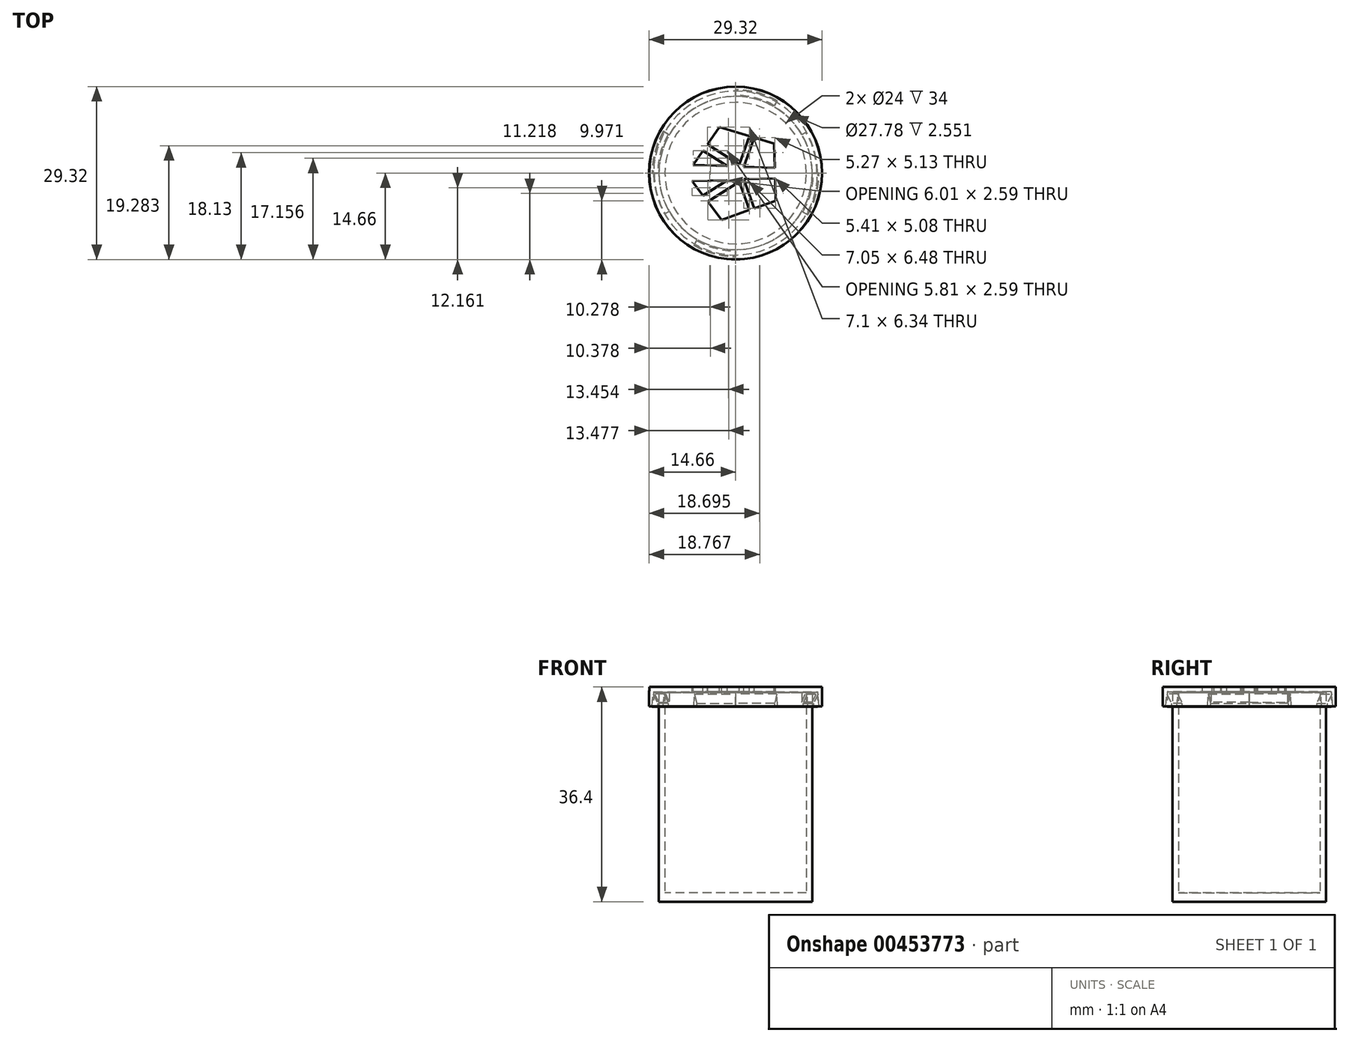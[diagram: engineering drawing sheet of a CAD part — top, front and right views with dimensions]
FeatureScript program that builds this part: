
annotation { "Feature Type Name" : "Feature", "Feature Type Description" : "" }
export const myFeature = defineFeature(function(context is Context, id is Id, definition is map)
    precondition{}
    {
        {
            var Q0;
            Q0=qCreatedBy(makeId("Front.planeOp"),FACE);
            var sketch = newSketch(context, id + "F0", { "sketchPlane" : qUnion([Q0])});
            skLineSegment(sketch, "E0", {"start": v(0, 34.9) * mm, "end": v(14.64, 34.9) * mm});
            skLineSegment(sketch, "E1", {"start": v(14.64, 34.9) * mm, "end": v(14.66, 31.61) * mm});
            skLineSegment(sketch, "E2", {"start": v(13.9, 31.58) * mm, "end": v(13.9, 34.13) * mm});
            skLineSegment(sketch, "E3", {"start": v(13.9, 34.13) * mm, "end": v(0, 34.13) * mm});
            skLineSegment(sketch, "E4", {"start": v(0, 34.13) * mm, "end": v(0, 34.9) * mm});
            skLineSegment(sketch, "E5", {"start": v(13.9, 31.58) * mm, "end": v(14.66, 31.61) * mm});
            skSolve(sketch);
        }
        {
            var Q0;
            Q0 = qSketchRegion(id + "F0", true);
            var Q1;
            Q1=sQuery(id+"F0.wireOp",EDGE,"E4");
            revolve(context, id + "F1", {"entities" : qUnion([Q0]), "axis" : qUnion([Q1]), "revolveType" : RevolveType.FULL});
        }
        {
            var Q0;
            Q0=qCreatedBy(makeId("Front.planeOp"),FACE);
            var sketch = newSketch(context, id + "F2", { "sketchPlane" : qUnion([Q0])});
            skLineSegment(sketch, "E6", {"start": v(14, 33.74) * mm, "end": v(13.2, 32.15) * mm});
            skLineSegment(sketch, "E7", {"start": v(13.2, 31.7) * mm, "end": v(14.15, 31.7) * mm});
            skLineSegment(sketch, "E8", {"start": v(14.15, 31.7) * mm, "end": v(14, 33.74) * mm});
            skLineSegment(sketch, "E9", {"start": v(13.2, 32.15) * mm, "end": v(13.2, 31.7) * mm});
            skLineSegment(sketch, "E10", {"start": v(0, 39.82) * mm, "end": v(0, 30.11) * mm, "construction": true});
            skSolve(sketch);
        }
        {
            var Q0;
            Q0 = qSketchRegion(id + "F2", true);
            var Q1;
            Q1=sQuery(id+"F2.wireOp",EDGE,"E10");
            revolve(context, id + "F3", {"entities" : qUnion([Q0]), "axis" : qUnion([Q1]), "revolveType" : RevolveType.ONE_DIRECTION, "angle" : 30 * degree});
        }
        {
            var Q0;
            Q0=qCreatedBy(makeId("Front.planeOp"),FACE);
            var sketch = newSketch(context, id + "F4", { "sketchPlane" : qUnion([Q0])});
            skLineSegment(sketch, "E11", {"start": v(0, 40.16) * mm, "end": v(0, 24.6) * mm, "construction": true});
            skSolve(sketch);
        }
        {
            var Q0;
            Q0=makeQuery(id+"F3.opRevolve","SWEPT_BODY",BODY,{"disambiguationData":[OSD([sQuery(id+"F2.wireOp",EDGE,"E6"),sQuery(id+"F2.wireOp",EDGE,"E7"),sQuery(id+"F2.wireOp",EDGE,"E8"),sQuery(id+"F2.wireOp",EDGE,"E9")])]});
            var Q1;
            Q1=sQuery(id+"F4.wireOp",EDGE,"E11");
            circularPattern(context, id + "F5", {"entities" : qUnion([Q0]), "axis" : qUnion([Q1]), "angle" : 360 * degree, "instanceCount" : 4, "equalSpace" : true});
        }
        {
            var Q0;
            Q0=makeQuery(id+"F1.opRevolve","SWEPT_FACE",FACE,{"disambiguationData":[OSD([sQuery(id+"F0.wireOp",EDGE,"E0")])]});
            var sketch = newSketch(context, id + "F6", { "sketchPlane" : qUnion([Q0])});
            skLineSegment(sketch, "E12.0", {"start": v(6.81, -4.69) * mm, "end": v(3.15, -5.98) * mm});
            skLineSegment(sketch, "E12.1", {"start": v(-2.35, -7.93) * mm, "end": v(-4.7, -4.85) * mm});
            skLineSegment(sketch, "E12.2", {"start": v(-7.19, 1.35) * mm, "end": v(-5.51, 3.8) * mm});
            skLineSegment(sketch, "E12.3", {"start": v(-2.76, 7.8) * mm, "end": v(2.35, 6.28) * mm});
            skLineSegment(sketch, "E12.4", {"start": v(6.56, 5.03) * mm, "end": v(6.67, 0.9) * mm});
            skPoint(sketch, "E12.0.midPoint", {"position": v(2.23, -6.3) * mm});
            skLineSegment(sketch, "E13", {"start": v(6.71, -0.9) * mm, "end": v(1.4, -1.04) * mm});
            skLineSegment(sketch, "E14", {"start": v(1.4, -1.04) * mm, "end": v(3.15, -5.98) * mm});
            skLineSegment(sketch, "E15", {"start": v(2.34, -6.27) * mm, "end": v(0.64, -1.45) * mm});
            skLineSegment(sketch, "E16", {"start": v(0.64, -1.45) * mm, "end": v(-4.7, -4.85) * mm});
            skLineSegment(sketch, "E17", {"start": v(-5.52, -3.8) * mm, "end": v(-1.38, -1.2) * mm});
            skLineSegment(sketch, "E18", {"start": v(-1.38, -1.2) * mm, "end": v(-7.39, -1.36) * mm});
            skLineSegment(sketch, "E19.MirrorCS", {"start": v(-5.51, 3.8) * mm, "end": v(-1.38, 1.2) * mm});
            skPoint(sketch, "E20.MirrorP", {"position": v(2.23, 6.3) * mm});
            skLineSegment(sketch, "E21.MirrorCS", {"start": v(2.35, 6.28) * mm, "end": v(0.64, 1.45) * mm});
            skLineSegment(sketch, "E22.MirrorCS", {"start": v(1.4, 1.04) * mm, "end": v(3.17, 6.04) * mm});
            skLineSegment(sketch, "E23.MirrorCS", {"start": v(0.64, 1.45) * mm, "end": v(-4.76, 4.89) * mm});
            skLineSegment(sketch, "E24.MirrorCS", {"start": v(-1.38, 1.2) * mm, "end": v(-7.19, 1.35) * mm});
            skLineSegment(sketch, "E25.MirrorCS", {"start": v(6.67, 0.9) * mm, "end": v(1.4, 1.04) * mm});
            skLineSegment(sketch, "E26.trimOffspring", {"start": v(2.34, -6.27) * mm, "end": v(-2.35, -7.93) * mm});
            skPoint(sketch, "E27.end.orphan", {"position": v(2.82, -7.62) * mm});
            skPoint(sketch, "E27.start.orphan", {"position": v(3.63, -7.34) * mm});
            skPoint(sketch, "E28.orphan", {"position": v(8, -0.87) * mm});
            skLineSegment(sketch, "E29.trimOffspring", {"start": v(6.71, -0.9) * mm, "end": v(6.81, -4.69) * mm});
            skArc(sketch, "E30.trimOffspring", {"start": v(2.23, -6.3) * mm, "mid": v(2.29, -6.29) * mm, "end": v(2.34, -6.27) * mm, "construction": true});
            skLineSegment(sketch, "E31.trimOffspring", {"start": v(-5.52, -3.8) * mm, "end": v(-7.39, -1.36) * mm});
            skPoint(sketch, "E32.end.orphan", {"position": v(-6.64, -4.5) * mm});
            skPoint(sketch, "E32.start.orphan", {"position": v(-6.2, -5.8) * mm});
            skPoint(sketch, "E33.orphan", {"position": v(-8.27, -0.21) * mm});
            skPoint(sketch, "E34.orphan", {"position": v(-8.58, 1.39) * mm});
            skPoint(sketch, "E35.orphan", {"position": v(-8.58, -1.39) * mm});
            skLineSegment(sketch, "E36.trimOffspring", {"start": v(-4.76, 4.89) * mm, "end": v(-2.76, 7.8) * mm});
            skPoint(sketch, "E37.MirrorCS.end.orphan", {"position": v(-6.64, 4.5) * mm});
            skPoint(sketch, "E37.MirrorCS.start.orphan", {"position": v(-6.2, 5.8) * mm});
            skLineSegment(sketch, "E38.trimOffspring", {"start": v(-5.51, 3.8) * mm, "end": v(-5.51, 3.8) * mm});
            skLineSegment(sketch, "E39.trimOffspring", {"start": v(3.17, 6.04) * mm, "end": v(6.56, 5.03) * mm});
            skPoint(sketch, "E40.MirrorCS.end.orphan", {"position": v(2.82, 7.62) * mm});
            skPoint(sketch, "E40.MirrorCS.start.orphan", {"position": v(3.63, 7.34) * mm});
            skPoint(sketch, "E41.orphan", {"position": v(8, 0.87) * mm});
            skSolve(sketch);
        }
        {
            var Q0;
            Q0 = qSketchRegion(id + "F6", true);
            extrude(context, id + "F7", {"entities" : qUnion([Q0]), "operationType" : NewBodyOperationType.REMOVE, "oppositeDirection" : true, "depth" : 10 * mm});
        }
        {
            var Q0;
            Q0=qCreatedBy(makeId("Top.planeOp"),FACE);
            var sketch = newSketch(context, id + "F8", { "sketchPlane" : qUnion([Q0])});
            skCircle(sketch, "E42", {"center": v(0, 0) * mm, "radius": 12 * mm});
            skCircle(sketch, "E43", {"center": v(0, 0) * mm, "radius": 13 * mm});
            skSolve(sketch);
        }
        {
            var Q0;
            Q0 = qSketchRegion(id + "F8", true);
            extrude(context, id + "F9", {"entities" : qUnion([Q0]), "depth" : 34 * mm});
        }
        {
            var Q0;
            Q0=qCreatedBy(makeId("Top.planeOp"),FACE);
            var sketch = newSketch(context, id + "F10", { "sketchPlane" : qUnion([Q0])});
            skCircle(sketch, "E44.0", {"center": v(0, 0) * mm, "radius": 13 * mm});
            skSolve(sketch);
        }
        {
            var Q0;
            Q0 = qSketchRegion(id + "F10", true);
            extrude(context, id + "F11", {"entities" : qUnion([Q0]), "operationType" : NewBodyOperationType.ADD, "oppositeDirection" : true, "depth" : 1.5 * mm});
        }
        {
            var Q0;
            Q0=qCreatedBy(makeId("Front.planeOp"),FACE);
            var sketch = newSketch(context, id + "F12", { "sketchPlane" : qUnion([Q0])});
            skLineSegment(sketch, "E45", {"start": v(12.95, 32.2) * mm, "end": v(13.8, 34) * mm});
            skLineSegment(sketch, "E46", {"start": v(13.8, 34) * mm, "end": v(12.66, 34) * mm});
            skLineSegment(sketch, "E47", {"start": v(12.66, 34) * mm, "end": v(12.95, 32.2) * mm});
            skLineSegment(sketch, "E48", {"start": v(0, 32.78) * mm, "end": v(0, 37.21) * mm, "construction": true});
            skSolve(sketch);
        }
        {
            var Q0;
            Q0 = qSketchRegion(id + "F12", true);
            var Q1;
            Q1=sQuery(id+"F12.wireOp",EDGE,"E48");
            revolve(context, id + "F13", {"operationType" : NewBodyOperationType.ADD, "entities" : qUnion([Q0]), "axis" : qUnion([Q1]), "revolveType" : RevolveType.ONE_DIRECTION, "angle" : 30 * degree});
        }
        {
            var Q0;
            Q0=qCreatedBy(makeId("Front.planeOp"),FACE);
            var sketch = newSketch(context, id + "F14", { "sketchPlane" : qUnion([Q0])});
            skLineSegment(sketch, "E49", {"start": v(0, 0) * mm, "end": v(0, 47.29) * mm, "construction": true});
            skSolve(sketch);
        }
        {
            var Q0;
            Q0=makeQuery(id+"F9.opExtrude","SWEPT_BODY",BODY,{"disambiguationData":[OSD([sQuery(id+"F8.wireOp",EDGE,"E42"),sQuery(id+"F8.wireOp",EDGE,"E43")])]});
            var Q1;
            Q1=sQuery(id+"F14.wireOp",EDGE,"E49");
            circularPattern(context, id + "F15", {"entities" : qUnion([Q0]), "axis" : qUnion([Q1]), "angle" : 360 * degree, "instanceCount" : 2, "equalSpace" : true});
        }
    });
